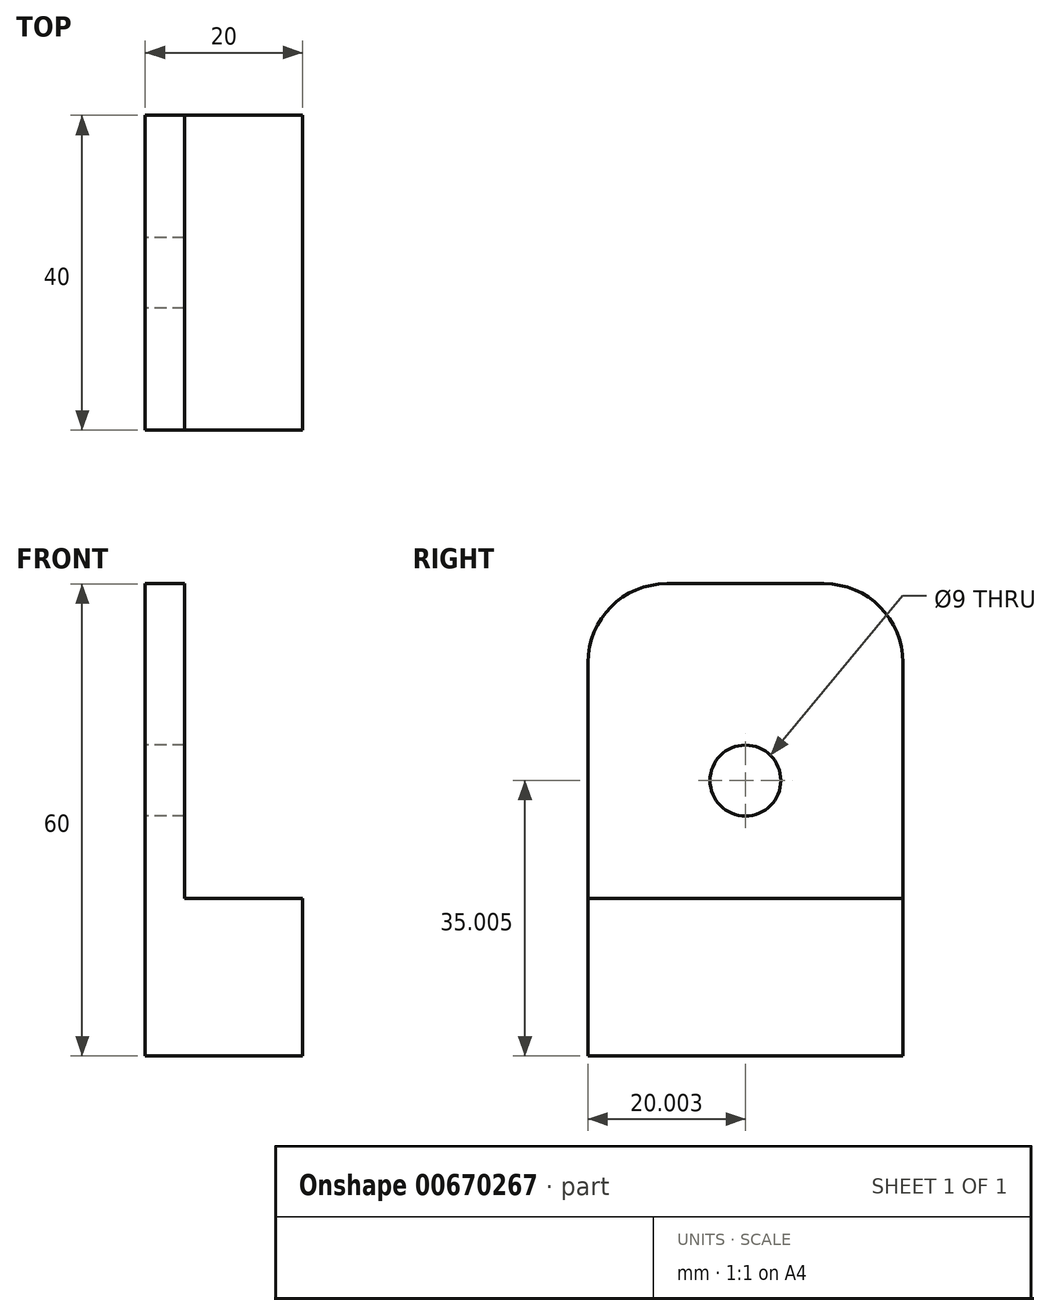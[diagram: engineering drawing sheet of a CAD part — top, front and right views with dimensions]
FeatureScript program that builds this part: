
annotation { "Feature Type Name" : "Feature", "Feature Type Description" : "" }
export const myFeature = defineFeature(function(context is Context, id is Id, definition is map)
    precondition{}
    {
        {
            var Q0;
            Q0=qCreatedBy(makeId("Right.planeOp"),FACE);
            var sketch = newSketch(context, id + "F0", { "sketchPlane" : qUnion([Q0])});
            skLineSegment(sketch, "E0.bottom", {"start": v(-8.27, 34.44) * mm, "end": v(11.73, 34.44) * mm});
            skLineSegment(sketch, "E0.top", {"start": v(-18.27, -25.56) * mm, "end": v(21.73, -25.56) * mm});
            skLineSegment(sketch, "E0.left", {"start": v(-18.27, 24.44) * mm, "end": v(-18.27, -25.56) * mm});
            skLineSegment(sketch, "E0.right", {"start": v(21.73, 24.44) * mm, "end": v(21.73, -25.56) * mm});
            skPoint(sketch, "E1.visualSharp", {"position": v(-18.27, 34.44) * mm});
            skArc(sketch, "E1.filletArc", {"start": v(-8.27, 34.44) * mm, "mid": v(-15.34, 31.52) * mm, "end": v(-18.27, 24.44) * mm});
            skPoint(sketch, "E2.visualSharp", {"position": v(21.73, 34.44) * mm});
            skArc(sketch, "E2.filletArc", {"start": v(21.73, 24.44) * mm, "mid": v(18.8, 31.52) * mm, "end": v(11.73, 34.44) * mm});
            skCircle(sketch, "E3", {"center": v(1.73, 9.44) * mm, "radius": 4.5 * mm});
            skSolve(sketch);
        }
        {
            var Q0;
            Q0=makeQuery(id+"F0.imprint","IMPRINT",FACE,{"disambiguationData":[TD([[makeQuery(id+"F0.imprint","IMPRINT",EDGE,{"derivedFrom":sQuery(id+"F0.wireOp",EDGE,"E0.bottom")}),-1.0]])]});
            extrude(context, id + "F1", {"entities" : qUnion([Q0]), "depth" : 5 * mm, "offsetDistance" : 25 * mm});
        }
        {
            var Q0;
            Q0=makeQuery(id+"F1.opExtrude","CAP_FACE",FACE,{"disambiguationData":[OSD([sQuery(id+"F0.wireOp",EDGE,"E0.bottom"),sQuery(id+"F0.wireOp",EDGE,"E0.top"),sQuery(id+"F0.wireOp",EDGE,"E0.left"),sQuery(id+"F0.wireOp",EDGE,"E0.right"),sQuery(id+"F0.wireOp",EDGE,"E1.filletArc"),sQuery(id+"F0.wireOp",EDGE,"E2.filletArc"),sQuery(id+"F0.wireOp",EDGE,"E3")])],"isStart":false});
            var sketch = newSketch(context, id + "F2", { "sketchPlane" : qUnion([Q0])});
            skLineSegment(sketch, "E4.bottom", {"start": v(-18.27, -25.56) * mm, "end": v(21.73, -25.56) * mm});
            skLineSegment(sketch, "E4.top", {"start": v(-18.27, -5.56) * mm, "end": v(21.73, -5.56) * mm});
            skLineSegment(sketch, "E4.left", {"start": v(-18.27, -25.56) * mm, "end": v(-18.27, -5.56) * mm});
            skLineSegment(sketch, "E4.right", {"start": v(21.73, -25.56) * mm, "end": v(21.73, -5.56) * mm});
            skSolve(sketch);
        }
        {
            var Q0;
            Q0=makeQuery(id+"F2.imprint","IMPRINT",FACE,{"disambiguationData":[TD([[makeQuery(id+"F2.imprint","IMPRINT",EDGE,{"derivedFrom":sQuery(id+"F2.wireOp",EDGE,"E4.bottom")}),1.0]])]});
            extrude(context, id + "F3", {"entities" : qUnion([Q0]), "operationType" : NewBodyOperationType.ADD, "depth" : 15 * mm, "offsetDistance" : 25 * mm});
        }
    });
